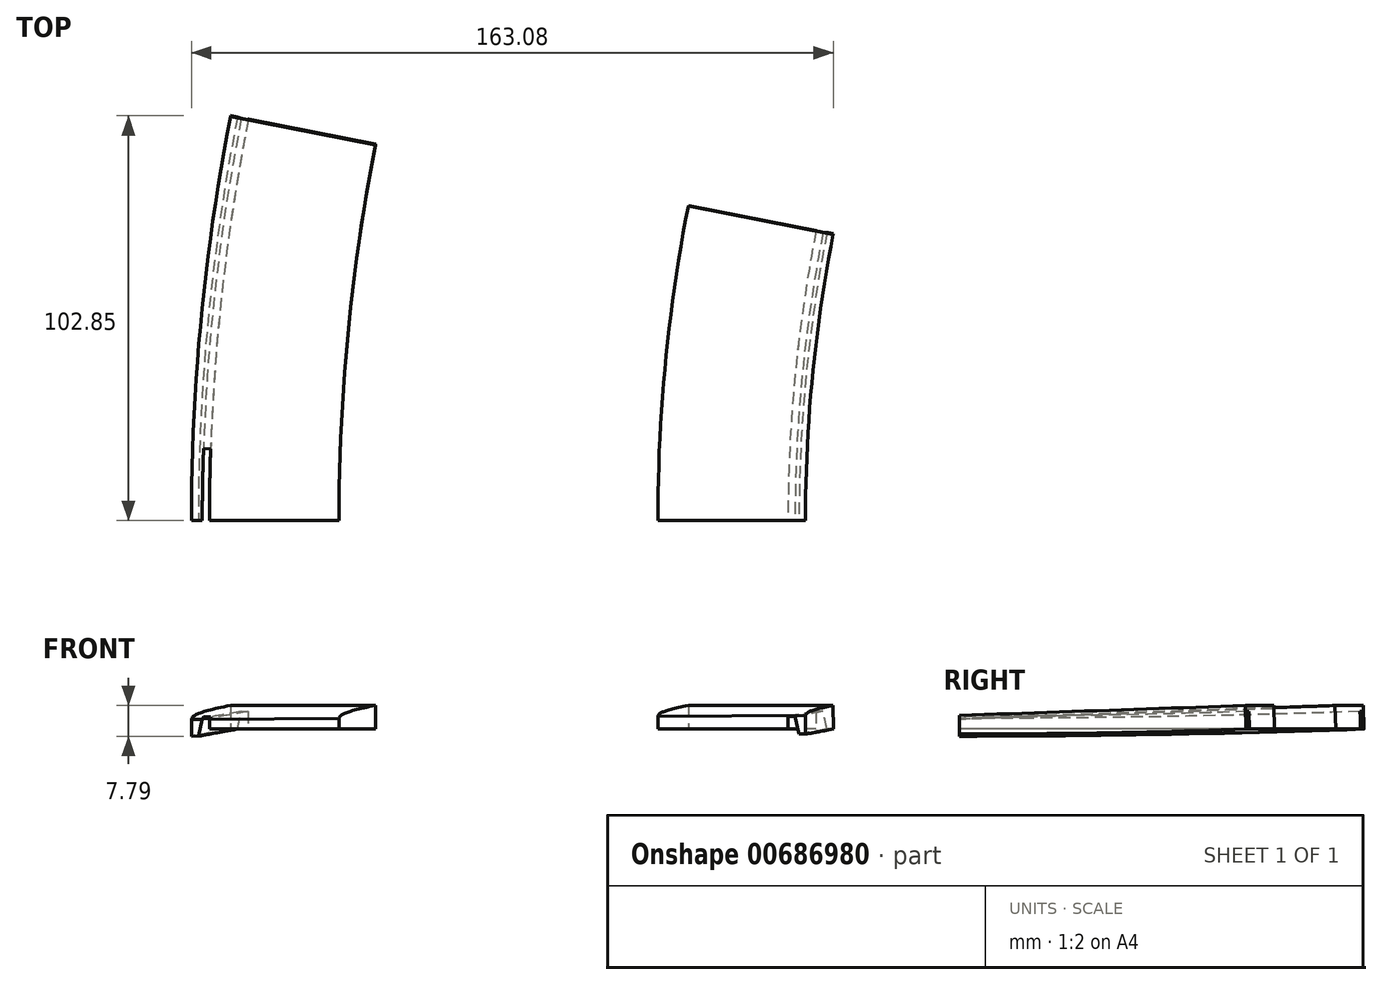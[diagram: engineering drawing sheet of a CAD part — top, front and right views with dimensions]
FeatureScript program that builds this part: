
annotation { "Feature Type Name" : "Feature", "Feature Type Description" : "" }
export const myFeature = defineFeature(function(context is Context, id is Id, definition is map)
    precondition{}
    {
        {
            var Q0;
            Q0=qCreatedBy(makeId("Front.planeOp"),FACE);
            var sketch = newSketch(context, id + "F0", { "sketchPlane" : qUnion([Q0])});
            skLineSegment(sketch, "E0", {"start": v(-0.07, -1.79) * mm, "end": v(534.04, 0) * mm});
            skLineSegment(sketch, "E1", {"start": v(534.04, 0) * mm, "end": v(517.63, 91.28) * mm});
            skLineSegment(sketch, "E2", {"start": v(517.63, 91.28) * mm, "end": v(-0.07, -1.79) * mm});
            skLineSegment(sketch, "E3", {"start": v(517.63, 91.28) * mm, "end": v(483.66, 280.23) * mm});
            skLineSegment(sketch, "E4", {"start": v(483.66, 280.23) * mm, "end": v(-34.04, 187.15) * mm});
            skArc(sketch, "E5", {"start": v(-34.04, 187.15) * mm, "mid": v(-22.42, 136.86) * mm, "end": v(-5.93, 87.94) * mm});
            skLineSegment(sketch, "E6", {"start": v(-5.93, 87.94) * mm, "end": v(483.66, 280.23) * mm});
            skLineSegment(sketch, "E7", {"start": v(-5.93, 87.94) * mm, "end": v(9.88, 0) * mm});
            skLineSegment(sketch, "E8", {"start": v(-0.07, -1.79) * mm, "end": v(0, -21.79) * mm});
            skLineSegment(sketch, "E9", {"start": v(0, -21.79) * mm, "end": v(156, -21.27) * mm});
            skLineSegment(sketch, "E10", {"start": v(156, -21.27) * mm, "end": v(155.93, -1.27) * mm});
            skLineSegment(sketch, "E11", {"start": v(118.43, -1.4) * mm, "end": v(118.5, -21.4) * mm});
            skLineSegment(sketch, "E12", {"start": v(37.43, -1.66) * mm, "end": v(37.5, -21.66) * mm});
            skSolve(sketch);
        }
        {
            var Q0;
            {var subQ0=sQuery(id+"F0.wireOp",EDGE,"E8");Q0=makeQuery(id+"F0.imprint","IMPRINT",FACE,{"disambiguationData":[TD([[makeQuery(id+"F0.imprint","IMPRINT",EDGE,{"derivedFrom":subQ0}),1.0]])]});}
            var Q1;
            {var subQ0=sQuery(id+"F0.wireOp",EDGE,"E10");Q1=makeQuery(id+"F0.imprint","IMPRINT",FACE,{"disambiguationData":[TD([[makeQuery(id+"F0.imprint","IMPRINT",EDGE,{"derivedFrom":subQ0}),1.0]])]});}
            var Q2;
            Q2=sQuery(id+"F0.wireOp",EDGE,"E1");
            revolve(context, id + "F1", {"entities" : qUnion([Q0, Q1]), "axis" : qUnion([Q2]), "revolveType" : RevolveType.SYMMETRIC, "angle" : 22.5 * degree});
        }
        {
            var Q0;
            Q0=qCreatedBy(makeId("Front.planeOp"),FACE);
            var sketch = newSketch(context, id + "F2", { "sketchPlane" : qUnion([Q0])});
            skLineSegment(sketch, "E13.bottom", {"start": v(4, -6.8) * mm, "end": v(152, -6.8) * mm});
            skLineSegment(sketch, "E13.top", {"start": v(4, -27.47) * mm, "end": v(152, -27.47) * mm});
            skLineSegment(sketch, "E13.left", {"start": v(4, -6.8) * mm, "end": v(4, -27.47) * mm});
            skLineSegment(sketch, "E13.right", {"start": v(152, -6.8) * mm, "end": v(152, -27.47) * mm});
            skLineSegment(sketch, "E14", {"start": v(526, 0) * mm, "end": v(526, -80.93) * mm});
            skSolve(sketch);
        }
        {
            var Q0;
            Q0=makeQuery(id+"F2.imprint","IMPRINT",FACE,{"disambiguationData":[TD([[makeQuery(id+"F2.imprint","IMPRINT",EDGE,{"derivedFrom":sQuery(id+"F2.wireOp",EDGE,"E13.bottom")}),-1.0]])]});
            var Q1;
            Q1=sQuery(id+"F2.wireOp",EDGE,"E14");
            revolve(context, id + "F3", {"operationType" : NewBodyOperationType.REMOVE, "entities" : qUnion([Q0]), "axis" : qUnion([Q1]), "revolveType" : RevolveType.FULL, "oppositeDirection" : true});
        }
        {
            var Q0;
            Q0=makeQuery(id+"F1.opRevolve","CAP_FACE",FACE,{"disambiguationData":[OSD([sQuery(id+"F0.wireOp",EDGE,"E0"),sQuery(id+"F0.wireOp",EDGE,"E9"),sQuery(id+"F0.wireOp",EDGE,"E10"),sQuery(id+"F0.wireOp",EDGE,"E11")])],"isStart":true});
            var sketch = newSketch(context, id + "F4", { "sketchPlane" : qUnion([Q0])});
            skLineSegment(sketch, "E15", {"start": v(-101.67, -3.65) * mm, "end": v(-179.14, -3.13) * mm});
            skLineSegment(sketch, "E16", {"start": v(-179.14, -3.13) * mm, "end": v(-179.14, 8.31) * mm});
            skLineSegment(sketch, "E17", {"start": v(-179.14, 8.31) * mm, "end": v(-102.53, 6.1) * mm});
            skLineSegment(sketch, "E18", {"start": v(-102.53, 6.1) * mm, "end": v(-101.67, -3.65) * mm});
            skSolve(sketch);
        }
        {
            var Q0;
            {var subQ0=sQuery(id+"F4.wireOp",EDGE,"E16");Q0=makeQuery(id+"F4.imprint","IMPRINT",FACE,{"disambiguationData":[TD([[makeQuery(id+"F4.imprint","IMPRINT",EDGE,{"derivedFrom":subQ0}),-1.0]])]});}
            var Q1;
            {var subQ4=sQuery(id+"F0.wireOp",EDGE,"E10");var subQ7=sQuery(id+"F0.wireOp",EDGE,"E0");var subQ8=makeQuery(id+"F1.opRevolve","CAP_EDGE",EDGE,{"disambiguationData":[OSD([subQ7]),TDD([makeQuery(id+"F0.imprint","IMPRINT",EDGE,{"disambiguationData":[TD([[makeQuery(id+"F0.imprint","INTERSECT",VERTEX,{"derivedFrom":[subQ7,subQ4]}),1.0]])],"derivedFrom":subQ7})])],"isStart":true});Q1=makeQuery(id+"F4.imprint","IMPRINT",FACE,{"disambiguationData":[TD([[makeQuery(id+"F4.imprint","IMPRINT",EDGE,{"derivedFrom":subQ8}),1.0]])]});}
            var Q2;
            Q2=makeQuery(id+"F4.imprint","IMPRINT",FACE,{"disambiguationData":[TD([[makeQuery(id+"F4.imprint","IMPRINT",EDGE,{"derivedFrom":sQuery(id+"F4.wireOp",EDGE,"xnwflF6W-fA75-Z1ex-eqH9-D9PAcPSBBPOl")}),-1.0]])]});
            extrude(context, id + "F5", {"entities" : qUnion([Q0, Q1, Q2]), "operationType" : NewBodyOperationType.REMOVE, "oppositeDirection" : true, "depth" : 211.4 * mm, "offsetDistance" : 25 * mm});
        }
        {
            var Q0;
            Q0=makeQuery(id+"F1.opRevolve","CAP_FACE",FACE,{"disambiguationData":[OSD([sQuery(id+"F0.wireOp",EDGE,"E0"),sQuery(id+"F0.wireOp",EDGE,"E8"),sQuery(id+"F0.wireOp",EDGE,"E9"),sQuery(id+"F0.wireOp",EDGE,"E12")])],"isStart":true});
            var sketch = newSketch(context, id + "F6", { "sketchPlane" : qUnion([Q0])});
            skLineSegment(sketch, "E19", {"start": v(35.84, -4.58) * mm, "end": v(-71.66, -3.86) * mm});
            skLineSegment(sketch, "E20", {"start": v(-71.66, -3.86) * mm, "end": v(-71.49, 21.2) * mm});
            skLineSegment(sketch, "E21", {"start": v(-71.49, 21.2) * mm, "end": v(37.5, 20.47) * mm});
            skLineSegment(sketch, "E22", {"start": v(37.5, 20.47) * mm, "end": v(35.84, -4.58) * mm});
            skSolve(sketch);
        }
        {
            var Q0;
            {var subQ0=sQuery(id+"F6.wireOp",EDGE,"E20");Q0=makeQuery(id+"F6.imprint","IMPRINT",FACE,{"disambiguationData":[TD([[makeQuery(id+"F6.imprint","IMPRINT",EDGE,{"derivedFrom":subQ0}),-1.0]])]});}
            var Q1;
            {var subQ4=sQuery(id+"F0.wireOp",EDGE,"E12");var subQ7=sQuery(id+"F0.wireOp",EDGE,"E0");var subQ8=makeQuery(id+"F1.opRevolve","CAP_EDGE",EDGE,{"disambiguationData":[OSD([subQ7]),TDD([makeQuery(id+"F0.imprint","IMPRINT",EDGE,{"disambiguationData":[TD([[makeQuery(id+"F0.imprint","INTERSECT",VERTEX,{"derivedFrom":[subQ7,subQ4]}),1.0]])],"derivedFrom":subQ7})])],"isStart":true});Q1=makeQuery(id+"F6.imprint","IMPRINT",FACE,{"disambiguationData":[TD([[makeQuery(id+"F6.imprint","IMPRINT",EDGE,{"derivedFrom":subQ8}),1.0]])]});}
            extrude(context, id + "F7", {"entities" : qUnion([Q0, Q1]), "operationType" : NewBodyOperationType.REMOVE, "oppositeDirection" : true, "depth" : 234.2 * mm, "offsetDistance" : 25 * mm});
        }
        {
            var Q0;
            Q0=qCreatedBy(makeId("Front.planeOp"),FACE);
            var sketch = newSketch(context, id + "F8", { "sketchPlane" : qUnion([Q0])});
            skLineSegment(sketch, "E23.bottom", {"start": v(202.69, 31.08) * mm, "end": v(-84.14, 31.08) * mm});
            skLineSegment(sketch, "E23.top", {"start": v(202.69, -68.38) * mm, "end": v(-84.14, -68.38) * mm});
            skLineSegment(sketch, "E23.left", {"start": v(202.69, 31.08) * mm, "end": v(202.69, -68.38) * mm});
            skLineSegment(sketch, "E23.right", {"start": v(-84.14, 31.08) * mm, "end": v(-84.14, -68.38) * mm});
            skSolve(sketch);
        }
        {
            var Q0;
            Q0=makeQuery(id+"F8.imprint","IMPRINT",FACE,{"disambiguationData":[TD([[makeQuery(id+"F8.imprint","IMPRINT",EDGE,{"derivedFrom":sQuery(id+"F8.wireOp",EDGE,"E23.bottom")}),1.0]])]});
            extrude(context, id + "F9", {"entities" : qUnion([Q0]), "operationType" : NewBodyOperationType.REMOVE, "depth" : 112 * mm, "offsetDistance" : 25 * mm});
        }
        {
            var Q0;
            Q0=qCreatedBy(makeId("Front.planeOp"),FACE);
            var sketch = newSketch(context, id + "F10", { "sketchPlane" : qUnion([Q0])});
            skLineSegment(sketch, "E24", {"start": v(0, -1.79) * mm, "end": v(534.11, 0) * mm});
            skLineSegment(sketch, "E25", {"start": v(534.11, 0) * mm, "end": v(517.7, 91.28) * mm});
            skLineSegment(sketch, "E26", {"start": v(517.7, 91.28) * mm, "end": v(0, -1.79) * mm});
            skLineSegment(sketch, "E27", {"start": v(517.7, 91.28) * mm, "end": v(475.67, 325.05) * mm});
            skLineSegment(sketch, "E28", {"start": v(475.67, 325.05) * mm, "end": v(-42.03, 231.97) * mm});
            skArc(sketch, "E29", {"start": v(-42.03, 231.97) * mm, "mid": v(-30.41, 181.68) * mm, "end": v(-13.92, 132.76) * mm});
            skLineSegment(sketch, "E30", {"start": v(-13.92, 132.76) * mm, "end": v(475.67, 325.05) * mm});
            skLineSegment(sketch, "E31", {"start": v(-13.92, 132.76) * mm, "end": v(9.95, 0) * mm});
            skLineSegment(sketch, "E32", {"start": v(0, -1.79) * mm, "end": v(0.07, -21.79) * mm});
            skLineSegment(sketch, "E33", {"start": v(0.07, -21.79) * mm, "end": v(156.07, -21.27) * mm});
            skLineSegment(sketch, "E34", {"start": v(156.07, -21.27) * mm, "end": v(156, -1.27) * mm});
            skLineSegment(sketch, "E35", {"start": v(0.02, -8.59) * mm, "end": v(1.72, -8.58) * mm});
            skLineSegment(sketch, "E36", {"start": v(1.72, -8.58) * mm, "end": v(2.72, -4.08) * mm});
            skLineSegment(sketch, "E37", {"start": v(2.72, -4.08) * mm, "end": v(4.52, -4.08) * mm});
            skLineSegment(sketch, "E38", {"start": v(4.52, -4.08) * mm, "end": v(4.58, -21.77) * mm});
            skLineSegment(sketch, "E39", {"start": v(156.02, -8.07) * mm, "end": v(154.32, -8.07) * mm});
            skLineSegment(sketch, "E40", {"start": v(154.32, -8.07) * mm, "end": v(153.32, -3.57) * mm});
            skLineSegment(sketch, "E41", {"start": v(153.32, -3.57) * mm, "end": v(151.52, -3.58) * mm});
            skLineSegment(sketch, "E42", {"start": v(151.52, -3.58) * mm, "end": v(151.58, -21.28) * mm});
            skLineSegment(sketch, "E43", {"start": v(0.02, -8.59) * mm, "end": v(-1.58, -8.23) * mm});
            skLineSegment(sketch, "E44", {"start": v(-1.58, -8.23) * mm, "end": v(-1.53, -23.12) * mm});
            skLineSegment(sketch, "E45", {"start": v(-1.53, -23.12) * mm, "end": v(0.07, -21.79) * mm});
            skSolve(sketch);
        }
        {
            var Q0;
            {var subQ0=sQuery(id+"F10.wireOp",EDGE,"E35");Q0=makeQuery(id+"F10.imprint","IMPRINT",FACE,{"disambiguationData":[TD([[makeQuery(id+"F10.imprint","IMPRINT",EDGE,{"derivedFrom":subQ0}),-1.0]])]});}
            var Q1;
            {var subQ0=sQuery(id+"F10.wireOp",EDGE,"E39");Q1=makeQuery(id+"F10.imprint","IMPRINT",FACE,{"disambiguationData":[TD([[makeQuery(id+"F10.imprint","IMPRINT",EDGE,{"derivedFrom":subQ0}),1.0]])]});}
            var Q2;
            {var subQ2=sQuery(id+"F10.wireOp",EDGE,"E43");Q2=makeQuery(id+"F10.imprint","IMPRINT",FACE,{"disambiguationData":[TD([[makeQuery(id+"F10.imprint","IMPRINT",EDGE,{"derivedFrom":subQ2}),1.0]])]});}
            var Q3;
            Q3=sQuery(id+"F10.wireOp",EDGE,"E25");
            revolve(context, id + "F11", {"operationType" : NewBodyOperationType.REMOVE, "entities" : qUnion([Q0, Q1, Q2]), "axis" : qUnion([Q3]), "revolveType" : RevolveType.ONE_DIRECTION, "oppositeDirection" : true, "angle" : 30 * degree});
        }
        {
            var Q0;
            Q0=qCreatedBy(makeId("Front.planeOp"),FACE);
            var sketch = newSketch(context, id + "F12", { "sketchPlane" : qUnion([Q0])});
            skLineSegment(sketch, "E46", {"start": v(0, -1.79) * mm, "end": v(534.11, 0) * mm});
            skLineSegment(sketch, "E47", {"start": v(534.11, 0) * mm, "end": v(517.7, 91.28) * mm});
            skLineSegment(sketch, "E48", {"start": v(517.7, 91.28) * mm, "end": v(0, -1.79) * mm});
            skLineSegment(sketch, "E49", {"start": v(517.7, 91.28) * mm, "end": v(465.88, 379.5) * mm});
            skLineSegment(sketch, "E50", {"start": v(465.88, 379.5) * mm, "end": v(-51.82, 286.43) * mm});
            skArc(sketch, "E51", {"start": v(-51.82, 286.43) * mm, "mid": v(-40.2, 236.13) * mm, "end": v(-23.71, 187.22) * mm});
            skLineSegment(sketch, "E52", {"start": v(-23.71, 187.22) * mm, "end": v(465.88, 379.5) * mm});
            skLineSegment(sketch, "E53", {"start": v(-23.71, 187.22) * mm, "end": v(9.95, 0) * mm});
            skLineSegment(sketch, "E54", {"start": v(0, -1.79) * mm, "end": v(0.07, -21.79) * mm});
            skLineSegment(sketch, "E55", {"start": v(0.07, -21.79) * mm, "end": v(156.07, -21.27) * mm});
            skLineSegment(sketch, "E56", {"start": v(156.07, -21.27) * mm, "end": v(156, -1.27) * mm});
            skLineSegment(sketch, "E57", {"start": v(0.02, -8.59) * mm, "end": v(1.72, -8.58) * mm});
            skLineSegment(sketch, "E58", {"start": v(1.72, -8.58) * mm, "end": v(2.72, -4.08) * mm});
            skLineSegment(sketch, "E59", {"start": v(2.72, -4.08) * mm, "end": v(4.52, -4.08) * mm});
            skLineSegment(sketch, "E60", {"start": v(4.52, -4.08) * mm, "end": v(4.58, -21.77) * mm});
            skLineSegment(sketch, "E61", {"start": v(156.02, -8.07) * mm, "end": v(154.32, -8.07) * mm});
            skLineSegment(sketch, "E62", {"start": v(154.32, -8.07) * mm, "end": v(153.32, -3.57) * mm});
            skLineSegment(sketch, "E63", {"start": v(153.32, -3.57) * mm, "end": v(151.52, -3.58) * mm});
            skLineSegment(sketch, "E64", {"start": v(151.52, -3.58) * mm, "end": v(151.58, -21.28) * mm});
            skLineSegment(sketch, "E65", {"start": v(2.72, -4.08) * mm, "end": v(2.7, 1.44) * mm});
            skLineSegment(sketch, "E66", {"start": v(4.52, -4.08) * mm, "end": v(4.52, 1.49) * mm});
            skLineSegment(sketch, "E67", {"start": v(4.52, 1.49) * mm, "end": v(2.7, 1.44) * mm});
            skSolve(sketch);
        }
        {
            var Q0;
            {var subQ5=sQuery(id+"F12.wireOp",EDGE,"E59");Q0=makeQuery(id+"F12.imprint","IMPRINT",FACE,{"disambiguationData":[TD([[makeQuery(id+"F12.imprint","IMPRINT",EDGE,{"derivedFrom":subQ5}),1.0]])]});}
            var Q1;
            Q1=sQuery(id+"F12.wireOp",EDGE,"E47");
            revolve(context, id + "F13", {"operationType" : NewBodyOperationType.REMOVE, "entities" : qUnion([Q0]), "axis" : qUnion([Q1]), "revolveType" : RevolveType.ONE_DIRECTION, "oppositeDirection" : true, "angle" : 2 * degree});
        }
    });
